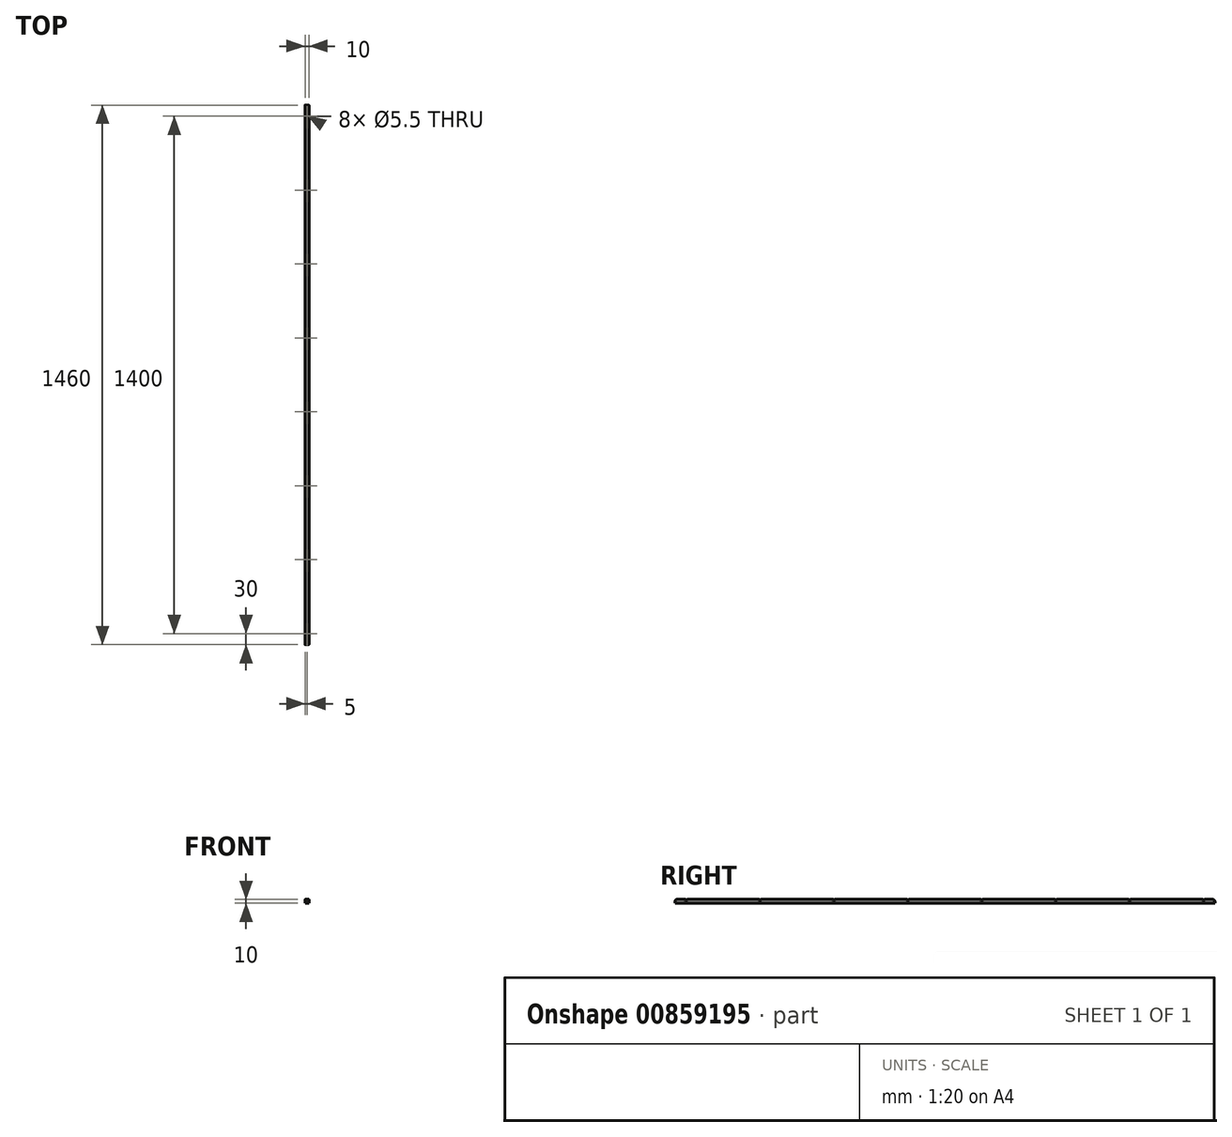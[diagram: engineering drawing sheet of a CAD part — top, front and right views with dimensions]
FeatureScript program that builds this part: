
annotation { "Feature Type Name" : "Feature", "Feature Type Description" : "" }
export const myFeature = defineFeature(function(context is Context, id is Id, definition is map)
    precondition{}
    {
        {
            var Q0;
            Q0=qCreatedBy(makeId("Front.planeOp"),FACE);
            var sketch = newSketch(context, id + "F0", { "sketchPlane" : qUnion([Q0])});
            skLineSegment(sketch, "E0.bottom", {"start": v(5, -5) * mm, "end": v(-5, -5) * mm});
            skLineSegment(sketch, "E0.top", {"start": v(5, 5) * mm, "end": v(-5, 5) * mm});
            skLineSegment(sketch, "E0.left", {"start": v(5, -5) * mm, "end": v(5, 5) * mm});
            skLineSegment(sketch, "E0.right", {"start": v(-5, -5) * mm, "end": v(-5, 5) * mm});
            skPoint(sketch, "E0.middle", {"position": v(0, 0) * mm});
            skSolve(sketch);
        }
        {
            var Q0;
            Q0=makeQuery(id+"F0.imprint","IMPRINT",FACE,{"disambiguationData":[TD([[makeQuery(id+"F0.imprint","IMPRINT",EDGE,{"derivedFrom":sQuery(id+"F0.wireOp",EDGE,"E0.bottom")}),-1.0]])]});
            extrude(context, id + "F1", {"entities" : qUnion([Q0]), "oppositeDirection" : true, "depth" : 1460 * mm, "offsetDistance" : 25 * mm});
        }
        {
            var Q0;
            Q0=makeQuery(id+"F1.opExtrude","SWEPT_FACE",FACE,{"disambiguationData":[OSD([sQuery(id+"F0.wireOp",EDGE,"E0.top")])]});
            var sketch = newSketch(context, id + "F2", { "sketchPlane" : qUnion([Q0])});
            skCircle(sketch, "E1", {"center": v(0, 30) * mm, "radius": 2.27 * mm});
            skPoint(sketch, "E1.centerSnap0", {"position": v(0, 0) * mm});
            skCircle(sketch, "E2.0.1.0", {"center": v(0, 230) * mm, "radius": 2.27 * mm});
            skCircle(sketch, "E2.0.2.0", {"center": v(0, 430) * mm, "radius": 2.27 * mm});
            skCircle(sketch, "E2.0.3.0", {"center": v(0, 630) * mm, "radius": 2.27 * mm});
            skCircle(sketch, "E2.0.4.0", {"center": v(0, 830) * mm, "radius": 2.27 * mm});
            skCircle(sketch, "E2.0.5.0", {"center": v(0, 1030) * mm, "radius": 2.27 * mm});
            skCircle(sketch, "E2.0.6.0", {"center": v(0, 1230) * mm, "radius": 2.27 * mm});
            skCircle(sketch, "E2.0.7.0", {"center": v(0, 1430) * mm, "radius": 2.27 * mm});
            skLineSegment(sketch, "E2.direction1", {"start": v(0, 30) * mm, "end": v(25, 30) * mm, "construction": true});
            skLineSegment(sketch, "E2.direction2", {"start": v(0, 30) * mm, "end": v(0, 230) * mm, "construction": true});
            skSolve(sketch);
        }
        {
            var Q0;
            Q0=sQuery(id+"F2.wireOp",VERTEX,"E2.direction1.start");
            var Q1;
            Q1=sQuery(id+"F2.wireOp",VERTEX,"E2.direction2.end");
            var Q2;
            Q2=sQuery(id+"F2.wireOp",VERTEX,"E2.0.2.0.center");
            var Q3;
            Q3=sQuery(id+"F2.wireOp",VERTEX,"E2.0.3.0.center");
            var Q4;
            Q4=sQuery(id+"F2.wireOp",VERTEX,"E2.0.4.0.center");
            var Q5;
            Q5=sQuery(id+"F2.wireOp",VERTEX,"E2.0.5.0.center");
            var Q6;
            Q6=sQuery(id+"F2.wireOp",VERTEX,"E2.0.6.0.center");
            var Q7;
            Q7=sQuery(id+"F2.wireOp",VERTEX,"E2.0.7.0.center");
            var Q8;
            Q8=sQuery(id+"F2.wireOp",VERTEX,"E2.0.8.0.center");
            var Q9;
            Q9=sQuery(id+"F2.wireOp",VERTEX,"86257c0e-1197-42b0-9796-6cbe976b8c1d.0.0.9.center");
            var Q10;
            Q10=makeQuery(id+"F1.opExtrude","SWEPT_BODY",BODY,{"disambiguationData":[OSD([sQuery(id+"F0.wireOp",EDGE,"E0.bottom"),sQuery(id+"F0.wireOp",EDGE,"E0.top"),sQuery(id+"F0.wireOp",EDGE,"E0.left"),sQuery(id+"F0.wireOp",EDGE,"E0.right")])]});
            hole(context, id + "F3", {"style" : HoleStyle.C_SINK, "endStyle" : HoleEndStyle.THROUGH, "standardTappedOrClearance" : lookupTablePath({ "fit" : "Normal", "standard" : "ISO", "size" : "M5", "type" : "Clearance" }), "standardBlindInLast" : lookupTablePath({ "fit" : "Standard", "standard" : "ISO", "size" : "M5", "type" : "Clearance" }), "holeDiameter" : 5.5 * mm, "cSinkDiameter" : 11.2 * mm, "cSinkAngle" : 90 * degree, "majorDiameter" : 5 * mm, "isTappedThrough" : true, "tappedDepth" : 12 * mm, "tapClearance" : 3, "locations" : qUnion([Q0, Q1, Q2, Q3, Q4, Q5, Q6, Q7, Q8, Q9]), "scope" : qUnion([Q10])});
        }
        {
            var Q0;
            Q0=makeQuery(id+"F1.opExtrude","CAP_EDGE",EDGE,{"disambiguationData":[OSD([sQuery(id+"F0.wireOp",EDGE,"E0.top")])],"isStart":false});
            fillet(context, id + "F4", {"entities" : qUnion([Q0]), "radius" : 5 * mm, "tangentPropagation" : true, "allowEdgeOverflow" : false});
        }
        {
            var Q0;
            Q0=makeQuery(id+"F1.opExtrude","CAP_EDGE",EDGE,{"disambiguationData":[OSD([sQuery(id+"F0.wireOp",EDGE,"E0.top")])],"isStart":true});
            fillet(context, id + "F5", {"entities" : qUnion([Q0]), "radius" : 5 * mm, "tangentPropagation" : true, "allowEdgeOverflow" : false});
        }
    });
